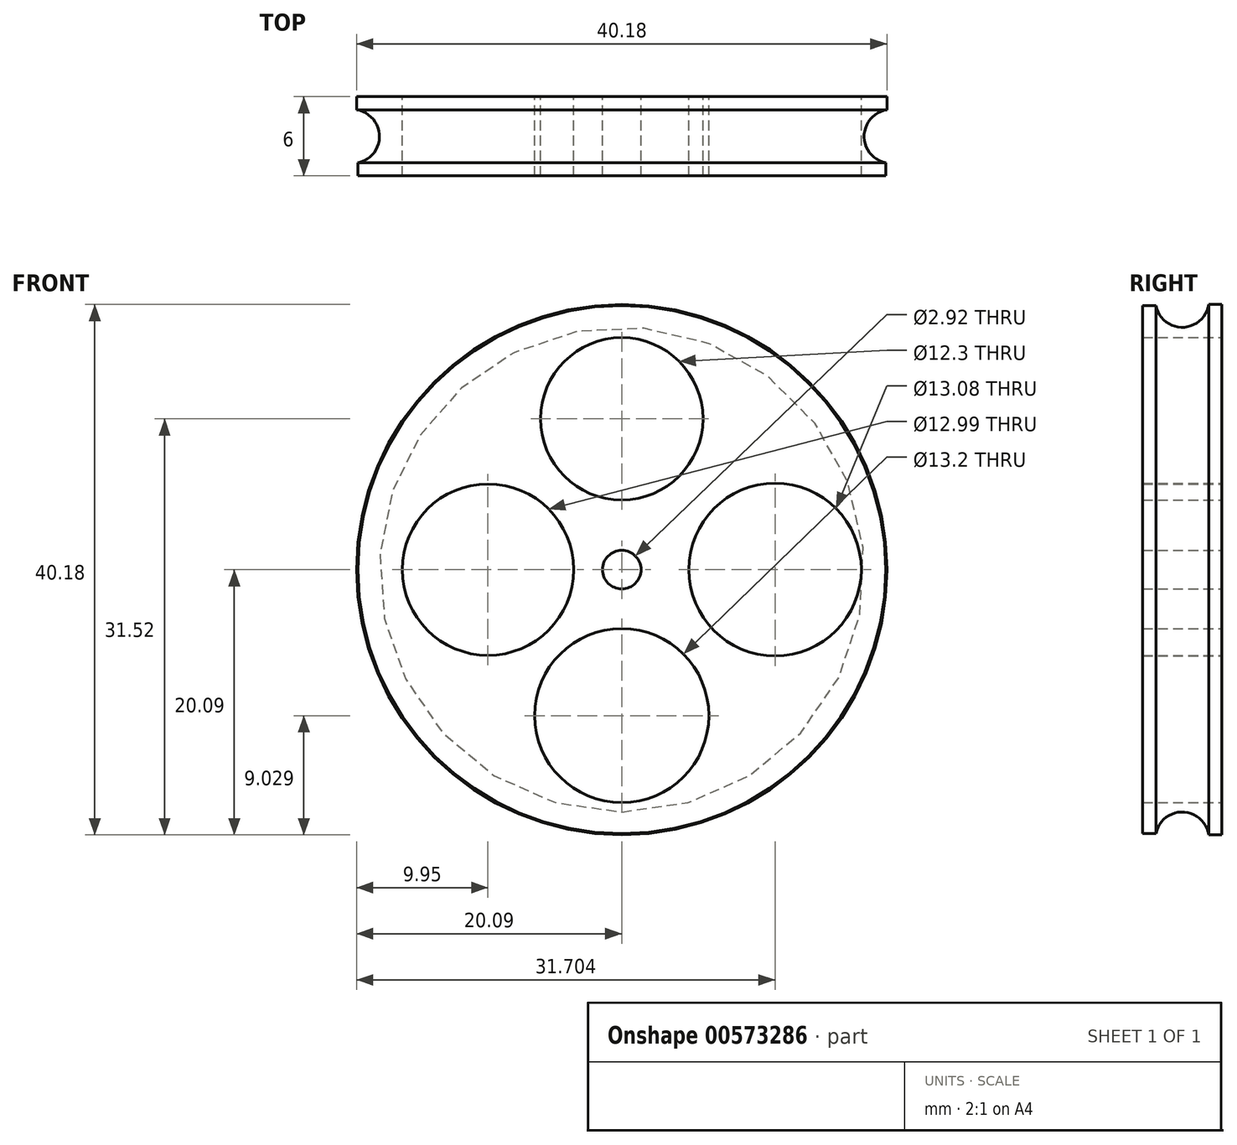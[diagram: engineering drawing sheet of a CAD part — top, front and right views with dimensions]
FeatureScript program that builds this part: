
annotation { "Feature Type Name" : "Feature", "Feature Type Description" : "" }
export const myFeature = defineFeature(function(context is Context, id is Id, definition is map)
    precondition{}
    {
        {
            var Q0;
            Q0=qCreatedBy(makeId("Right.planeOp"),FACE);
            var sketch = newSketch(context, id + "F0", { "sketchPlane" : qUnion([Q0])});
            skLineSegment(sketch, "E0.left", {"start": v(0, 0) * mm, "end": v(0, 0) * mm});
            skLineSegment(sketch, "E0.right", {"start": v(3, 0) * mm, "end": v(3, 0) * mm});
            skLineSegment(sketch, "E1.right", {"start": v(-3, 0) * mm, "end": v(-3, 0) * mm});
            skLineSegment(sketch, "E2", {"start": v(-3, 0) * mm, "end": v(-3, 20) * mm});
            skLineSegment(sketch, "E3", {"start": v(3, 20.1) * mm, "end": v(3, 0) * mm});
            skLineSegment(sketch, "E4", {"start": v(-3, 20) * mm, "end": v(-2, 20) * mm});
            skLineSegment(sketch, "E5", {"start": v(3, 20.1) * mm, "end": v(2, 20.1) * mm});
            skArc(sketch, "E6", {"start": v(-2, 20) * mm, "mid": v(0.04, 18.36) * mm, "end": v(2, 20.1) * mm});
            skLineSegment(sketch, "E7", {"start": v(-3, 0) * mm, "end": v(3, 0) * mm});
            skSolve(sketch);
        }
        {
            var Q0;
            Q0 = qSketchRegion(id + "F0", true);
            var Q1;
            Q1=sQuery(id+"F0.wireOp",EDGE,"E7");
            revolve(context, id + "F1", {"entities" : qUnion([Q0]), "axis" : qUnion([Q1]), "revolveType" : RevolveType.FULL});
        }
        {
            var Q0;
            Q0=qCreatedBy(makeId("Front.planeOp"),FACE);
            var sketch = newSketch(context, id + "F2", { "sketchPlane" : qUnion([Q0])});
            skCircle(sketch, "E8", {"center": v(0, 0) * mm, "radius": 1.46 * mm});
            skSolve(sketch);
        }
        {
            var Q0;
            Q0=makeQuery(id+"F2.imprint","IMPRINT",FACE,{"disambiguationData":[TD([[makeQuery(id+"F2.imprint","IMPRINT",EDGE,{"derivedFrom":sQuery(id+"F2.wireOp",EDGE,"E8")}),1.0]])]});
            extrude(context, id + "F3", {"entities" : qUnion([Q0]), "depth" : 23.42 * mm, "offsetDistance" : 25.4 * mm, "hasSecondDirection" : true, "secondDirectionOppositeDirection" : true, "secondDirectionDepth" : 25.4 * mm});
        }
        {
            var Q0;
            Q0=makeQuery(id+"F3.opExtrude","SWEPT_BODY",BODY,{"disambiguationData":[OSD([sQuery(id+"F2.wireOp",EDGE,"E8")])]});
            var Q1;
            Q1=makeQuery(id+"F1.opRevolve","SWEPT_BODY",BODY,{"disambiguationData":[OSD([sQuery(id+"F0.wireOp",EDGE,"E2"),sQuery(id+"F0.wireOp",EDGE,"E3"),sQuery(id+"F0.wireOp",EDGE,"E4"),sQuery(id+"F0.wireOp",EDGE,"E5"),sQuery(id+"F0.wireOp",EDGE,"E6"),sQuery(id+"F0.wireOp",EDGE,"E7")])]});
            booleanBodies(context, id + "F4", {"operationType" : BooleanOperationType.SUBTRACTION, "tools" : qUnion([Q0]), "targets" : qUnion([Q1])});
        }
        {
            var Q0;
            Q0=qCreatedBy(makeId("Front.planeOp"),FACE);
            var sketch = newSketch(context, id + "F5", { "sketchPlane" : qUnion([Q0])});
            skCircle(sketch, "E9", {"center": v(0, 11.43) * mm, "radius": 6.15 * mm});
            skCircle(sketch, "E10", {"center": v(-10.14, 0) * mm, "radius": 6.5 * mm});
            skCircle(sketch, "E11", {"center": v(0, -11.06) * mm, "radius": 6.6 * mm});
            skCircle(sketch, "E12", {"center": v(11.61, 0) * mm, "radius": 6.54 * mm});
            skSolve(sketch);
        }
        {
            var Q0;
            Q0=makeQuery(id+"F5.imprint","IMPRINT",FACE,{"disambiguationData":[TD([[makeQuery(id+"F5.imprint","IMPRINT",EDGE,{"derivedFrom":sQuery(id+"F5.wireOp",EDGE,"E9")}),1.0]])]});
            var Q1;
            Q1=makeQuery(id+"F5.imprint","IMPRINT",FACE,{"disambiguationData":[TD([[makeQuery(id+"F5.imprint","IMPRINT",EDGE,{"derivedFrom":sQuery(id+"F5.wireOp",EDGE,"E10")}),1.0]])]});
            var Q2;
            Q2=makeQuery(id+"F5.imprint","IMPRINT",FACE,{"disambiguationData":[TD([[makeQuery(id+"F5.imprint","IMPRINT",EDGE,{"derivedFrom":sQuery(id+"F5.wireOp",EDGE,"E11")}),1.0]])]});
            var Q3;
            Q3=makeQuery(id+"F5.imprint","IMPRINT",FACE,{"disambiguationData":[TD([[makeQuery(id+"F5.imprint","IMPRINT",EDGE,{"derivedFrom":sQuery(id+"F5.wireOp",EDGE,"E12")}),1.0]])]});
            extrude(context, id + "F6", {"entities" : qUnion([Q0, Q1, Q2, Q3]), "depth" : 38.6 * mm, "offsetDistance" : 25.4 * mm, "hasSecondDirection" : true, "secondDirectionOppositeDirection" : true, "secondDirectionDepth" : 35.81 * mm});
        }
        {
            var Q0;
            Q0=makeQuery(id+"F6.opExtrude","SWEPT_BODY",BODY,{"disambiguationData":[OSD([sQuery(id+"F5.wireOp",EDGE,"E9")])]});
            var Q1;
            Q1=makeQuery(id+"F6.opExtrude","SWEPT_BODY",BODY,{"disambiguationData":[OSD([sQuery(id+"F5.wireOp",EDGE,"E10")])]});
            var Q2;
            Q2=makeQuery(id+"F6.opExtrude","SWEPT_BODY",BODY,{"disambiguationData":[OSD([sQuery(id+"F5.wireOp",EDGE,"E11")])]});
            var Q3;
            Q3=makeQuery(id+"F6.opExtrude","SWEPT_BODY",BODY,{"disambiguationData":[OSD([sQuery(id+"F5.wireOp",EDGE,"E12")])]});
            var Q4;
            Q4=makeQuery(id+"F1.opRevolve","SWEPT_BODY",BODY,{"disambiguationData":[OSD([sQuery(id+"F0.wireOp",EDGE,"E2"),sQuery(id+"F0.wireOp",EDGE,"E3"),sQuery(id+"F0.wireOp",EDGE,"E4"),sQuery(id+"F0.wireOp",EDGE,"E5"),sQuery(id+"F0.wireOp",EDGE,"E6"),sQuery(id+"F0.wireOp",EDGE,"E7")])]});
            booleanBodies(context, id + "F7", {"operationType" : BooleanOperationType.SUBTRACTION, "tools" : qUnion([Q0, Q1, Q2, Q3]), "targets" : qUnion([Q4])});
        }
    });
